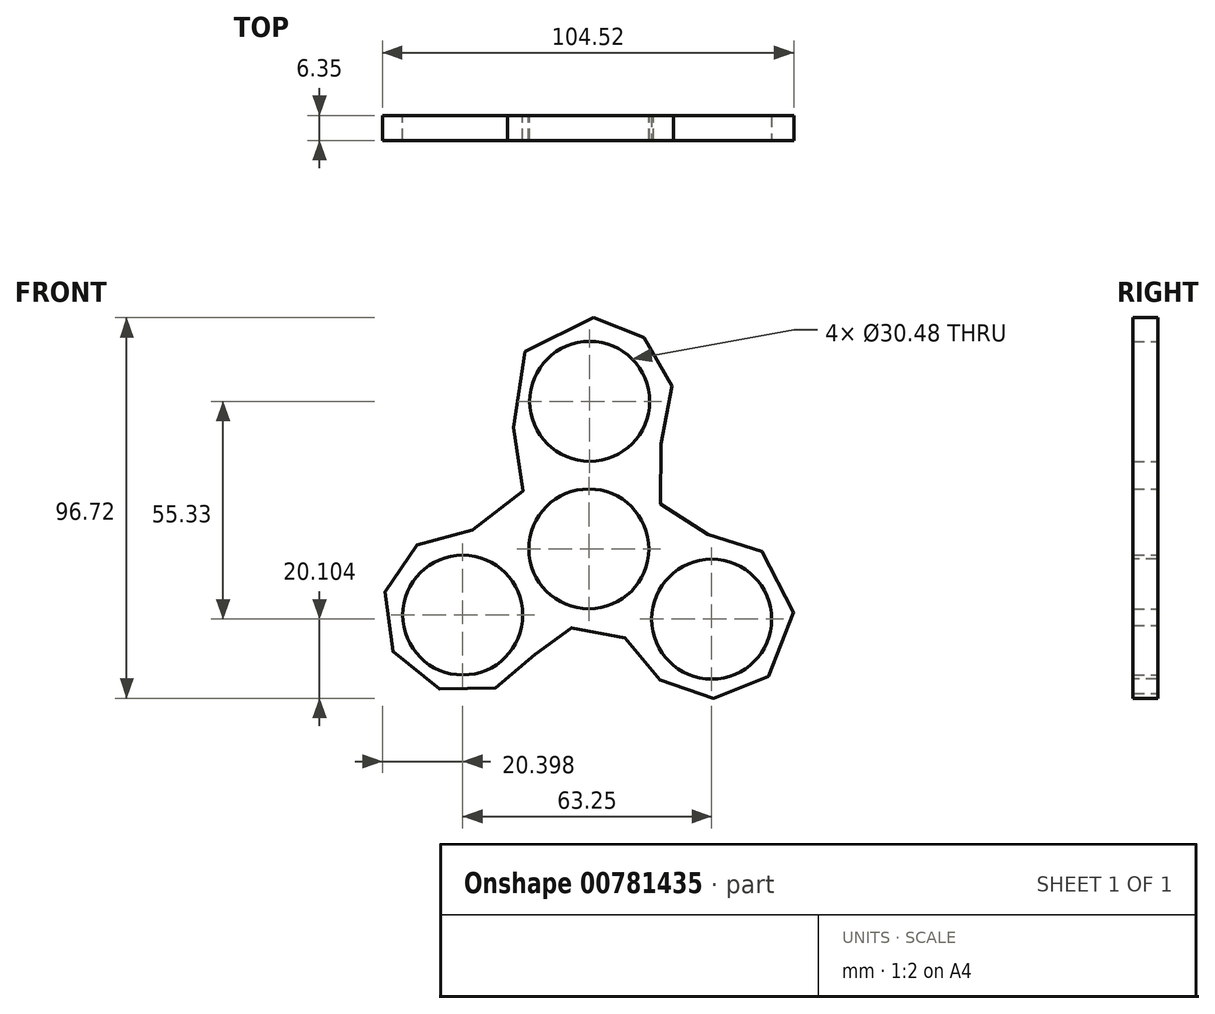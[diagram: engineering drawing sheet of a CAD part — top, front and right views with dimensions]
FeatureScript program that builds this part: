
annotation { "Feature Type Name" : "Feature", "Feature Type Description" : "" }
export const myFeature = defineFeature(function(context is Context, id is Id, definition is map)
    precondition{}
    {
        {
            var Q0;
            Q0=qCreatedBy(makeId("Front.planeOp"),FACE);
            var sketch = newSketch(context, id + "F0", { "sketchPlane" : qUnion([Q0])});
            skFitSpline(sketch, "E0", {"points": [v(0, 48.66) * mm, v(-11.25, 45.47) * mm, v(-19.61, 36.32) * mm, v(-21.47, 23.7) * mm, v(-17.36, 14.68) * mm, v(-17.1, 6.86) * mm, v(-22.06, -1.35) * mm, v(-29, -5.01) * mm, v(-36.43, -5.62) * mm, v(-41.95, -7.35) * mm, v(-48.43, -12.15) * mm, v(-51.72, -17.4) * mm, v(-53.45, -22.88) * mm, v(-53.13, -30.7) * mm, v(-50.3, -37.32) * mm, v(-45.4, -42.6) * mm, v(-38.95, -45.78) * mm, v(-33.13, -46.81) * mm, v(-26.38, -45.87) * mm, v(-20.28, -42.87) * mm, v(-15.82, -38.56) * mm, v(-14.65, -36.44) * mm, v(-11.46, -33.02) * mm, v(-8.05, -30.94) * mm, v(-4.16, -29.8) * mm, v(1.52, -29.9) * mm, v(8.14, -32.9) * mm, v(11.6, -36.85) * mm, v(15.08, -41.87) * mm, v(20.85, -45.81) * mm, v(26.1, -47.69) * mm, v(33.2, -47.88) * mm, v(39.25, -45.95) * mm, v(45.73, -41.09) * mm, v(50.3, -32.5) * mm, v(50.2, -22.45) * mm, v(45.96, -13.86) * mm, v(38.82, -8.28) * mm, v(32, -6.6) * mm, v(28.1, -6.27) * mm, v(21.97, -3.93) * mm, v(17.06, 1.2) * mm, v(15.16, 7.57) * mm, v(16.65, 15.66) * mm, v(19.19, 20.63) * mm, v(20.22, 28.9) * mm, v(18.44, 35.74) * mm, v(15.73, 40.48) * mm, v(10.48, 45.27) * mm, v(4.85, 47.62) * mm, v(0, 48.66) * mm]});
            skSolve(sketch);
        }
        {
            var Q0;
            Q0=makeQuery(id+"F0.imprint","IMPRINT",FACE,{"disambiguationData":[TD([[makeQuery(id+"F0.imprint","IMPRINT",EDGE,{"derivedFrom":sQuery(id+"F0.wireOp",EDGE,"E0")}),1.0]])]});
            var sketch = newSketch(context, id + "F1", { "sketchPlane" : qUnion([Q0])});
            skCircle(sketch, "E1", {"center": v(-33.26, -26.9) * mm, "radius": 15.02 * mm});
            skSolve(sketch);
        }
        {
            var Q0;
            Q0=makeQuery(id+"F0.imprint","IMPRINT",FACE,{"disambiguationData":[TD([[makeQuery(id+"F0.imprint","IMPRINT",EDGE,{"derivedFrom":sQuery(id+"F0.wireOp",EDGE,"E0")}),1.0]])]});
            var sketch = newSketch(context, id + "F2", { "sketchPlane" : qUnion([Q0])});
            skCircle(sketch, "E2", {"center": v(-1, 27.37) * mm, "radius": 14.89 * mm});
            skSolve(sketch);
        }
        {
            var Q0;
            Q0=makeQuery(id+"F0.imprint","IMPRINT",FACE,{"disambiguationData":[TD([[makeQuery(id+"F0.imprint","IMPRINT",EDGE,{"derivedFrom":sQuery(id+"F0.wireOp",EDGE,"E0")}),1.0]])]});
            var sketch = newSketch(context, id + "F3", { "sketchPlane" : qUnion([Q0])});
            skCircle(sketch, "E3", {"center": v(-1.21, -10.1) * mm, "radius": 15.82 * mm});
            skSolve(sketch);
        }
        {
            var Q0;
            Q0=makeQuery(id+"F0.imprint","IMPRINT",FACE,{"disambiguationData":[TD([[makeQuery(id+"F0.imprint","IMPRINT",EDGE,{"derivedFrom":sQuery(id+"F0.wireOp",EDGE,"E0")}),1.0]])]});
            extrude(context, id + "F4", {"entities" : qUnion([Q0]), "depth" : 6.35 * mm, "offsetDistance" : 25.4 * mm});
        }
        {
            var Q0;
            Q0=sQuery(id+"F1.wireOp",VERTEX,"E1.center");
            var Q1;
            Q1=makeQuery(id+"F4.opExtrude","SWEPT_BODY",BODY,{"disambiguationData":[OSD([sQuery(id+"F0.wireOp",EDGE,"E0")])]});
            hole(context, id + "F5", {"style" : HoleStyle.SIMPLE, "endStyle" : HoleEndStyle.THROUGH, "oppositeDirection" : true, "holeDiameter" : 30.48 * mm, "majorDiameter" : 6.35 * mm, "isTappedThrough" : true, "tappedDepth" : 12.7 * mm, "tapClearance" : 3, "locations" : qUnion([Q0]), "scope" : qUnion([Q1])});
        }
        {
            var Q0;
            Q0=makeQuery(id+"F4.opExtrude","CAP_FACE",FACE,{"disambiguationData":[OSD([sQuery(id+"F0.wireOp",EDGE,"E0")])],"isStart":false});
            var sketch = newSketch(context, id + "F6", { "sketchPlane" : qUnion([Q0])});
            skCircle(sketch, "E4", {"center": v(29.99, -27.96) * mm, "radius": 15.09 * mm});
            skSolve(sketch);
        }
        {
            var Q0;
            Q0=sQuery(id+"F2.wireOp",VERTEX,"E2.center");
            var Q1;
            Q1=makeQuery(id+"F4.opExtrude","SWEPT_BODY",BODY,{"disambiguationData":[OSD([sQuery(id+"F0.wireOp",EDGE,"E0")])]});
            hole(context, id + "F7", {"style" : HoleStyle.SIMPLE, "endStyle" : HoleEndStyle.THROUGH, "oppositeDirection" : true, "holeDiameter" : 30.48 * mm, "majorDiameter" : 6.35 * mm, "isTappedThrough" : true, "tappedDepth" : 12.7 * mm, "tapClearance" : 3, "locations" : qUnion([Q0]), "scope" : qUnion([Q1])});
        }
        {
            var Q0;
            Q0=sQuery(id+"F6.wireOp",VERTEX,"E4.center");
            var Q1;
            Q1=makeQuery(id+"F4.opExtrude","SWEPT_BODY",BODY,{"disambiguationData":[OSD([sQuery(id+"F0.wireOp",EDGE,"E0")])]});
            hole(context, id + "F8", {"style" : HoleStyle.SIMPLE, "endStyle" : HoleEndStyle.THROUGH, "holeDiameter" : 30.48 * mm, "majorDiameter" : 6.35 * mm, "isTappedThrough" : true, "tappedDepth" : 12.7 * mm, "tapClearance" : 3, "locations" : qUnion([Q0]), "scope" : qUnion([Q1])});
        }
        {
            var Q0;
            Q0=sQuery(id+"F3.wireOp",VERTEX,"E3.center");
            var Q1;
            Q1=makeQuery(id+"F4.opExtrude","SWEPT_BODY",BODY,{"disambiguationData":[OSD([sQuery(id+"F0.wireOp",EDGE,"E0")])]});
            hole(context, id + "F9", {"style" : HoleStyle.SIMPLE, "endStyle" : HoleEndStyle.THROUGH, "oppositeDirection" : true, "holeDiameter" : 30.48 * mm, "majorDiameter" : 6.35 * mm, "isTappedThrough" : true, "tappedDepth" : 12.7 * mm, "tapClearance" : 3, "locations" : qUnion([Q0]), "scope" : qUnion([Q1])});
        }
    });
